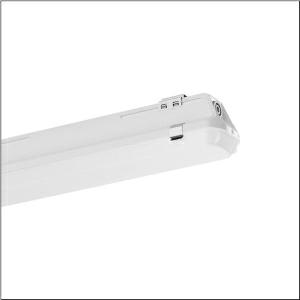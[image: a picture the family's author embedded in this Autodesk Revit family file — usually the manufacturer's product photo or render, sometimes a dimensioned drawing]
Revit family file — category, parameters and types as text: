
# Revit family: monsun_r__21_chemical_51fb30dp460b_d38f
name_source: partatom
category: Lighting Fixtures
units: mm (PartAtom-declared; Revit-internal decimal feet)

## family parameters
Cut with Voids When Loaded = No
Host = Face
Light Source = No
Part Type = Normal
Room Calculation Point = No
Round Connector Dimension = Use Diameter
Shared = No

## types (1)
- --- (1 x LED, 5740 lm, 39.4 W, 4000K)
    Apparent Load = 39 VA
    CIE Flux Codes = 48 77 93 95 100
    Color Rendering = 80
    Color Temperature = 4000K
    Default Elevation = 1800 mm
    Description = Monsun® 21 chemical, damp-proof luminaire, chain hanger, primary optical cover: enclosure, of PA, light emission: direct distribution, primary light characteristic: symmetric, installation type: suspended mounting, surface-mounted, horizontal mounting, vertical mounting, LED, rated luminous flux: 5.740lm, luminous efficacy: 146lm/W, light colour: 840, colour temperature: 4000K, control gear: ECG DALI, with terminal, 5-pole, max. 2.5mm², mains connection: 220..240V, AC, 50/60Hz, rated input power: 39W, housing, of glass-fibre reinforced polyester, uncoated, bright grey, incl. chain hanger, length: 1.590mm, width: 90mm, height: 88mm, clip for enclosure, of stainless steel (V2A), ceiling mounting element, of stainless steel (V2A), chain hanger, of stainless steel (V2A), protection rating (complete): IP66, insulation class (complete): insulation class I (protective earthing), certification: CE, ENEC, VDE, UKCA, protection symbol: D, impact resistance: IK08, permissible operating ambient temperature: -25..+35°C, standard: EN 50419, EN 60598-2-1, corresponds to IFS (International Featured Standards) requirements for safety and quality in the food industry, for indoor or canopied outdoor use, no direct snow, no direct sun, no direct rain, contact your sales advisor before using the luminaires in applications with unclear chemical exposure, large temperature fluctuations or condensation-forming humidity, LABS conformity tested according to VDMA 24364:2018-05, packaging unit: 1 piece
    Height = 89 mm
    Lamp = 1 x LED
    Lamp Light Flux = 5740 lm
    Lamp Power = 39.4 W
    Lamp count = 1
    Length = 1590 mm
    Luminous efficacy = 146 lm/W
    Manufacturer = Siteco
    ModVariant = No
    Model = 51FB30DP460B
    Mounting Place = Ceiling
    Mounting Type = Surface mounted
    Number of Poles = 1
    OnlyDefault = Yes
    Power Factor = 1
    Product Name = Monsun® 21 chemical
    Product group = damp-proof luminaire
    ProductGroupID = 301
    Protection Class = Protection class I
    Protection Degree = IP 66
    RLX_Detail_Level = 1
    RLX_Emergency_Light_Flux = 0 lm
    RLX_Emergency_Type = 0
    RLX_Emergency_Type_DB = No
    RlxData = <blob elided: 92413 chars, md5=b26157be>
    Socket = socket
    Standby Power = 0 W
    System Light Flux = 5740 lm
    System Power = 39 W
    Type Comments = factory setting: luminous flux: 100 % | dim-lin: 254 | 261 mA
    Type Image = l_1006717.jpg
    URL = http://relux.com
    VarID = @adj_152193
    Voltage = 0 V
    Weight = 0.00 kg
    Width = 90 mm

## geometry (parser evidence)
native form markers: Blend x4, Sweep x11
no freeform markers — native parametric forms only
